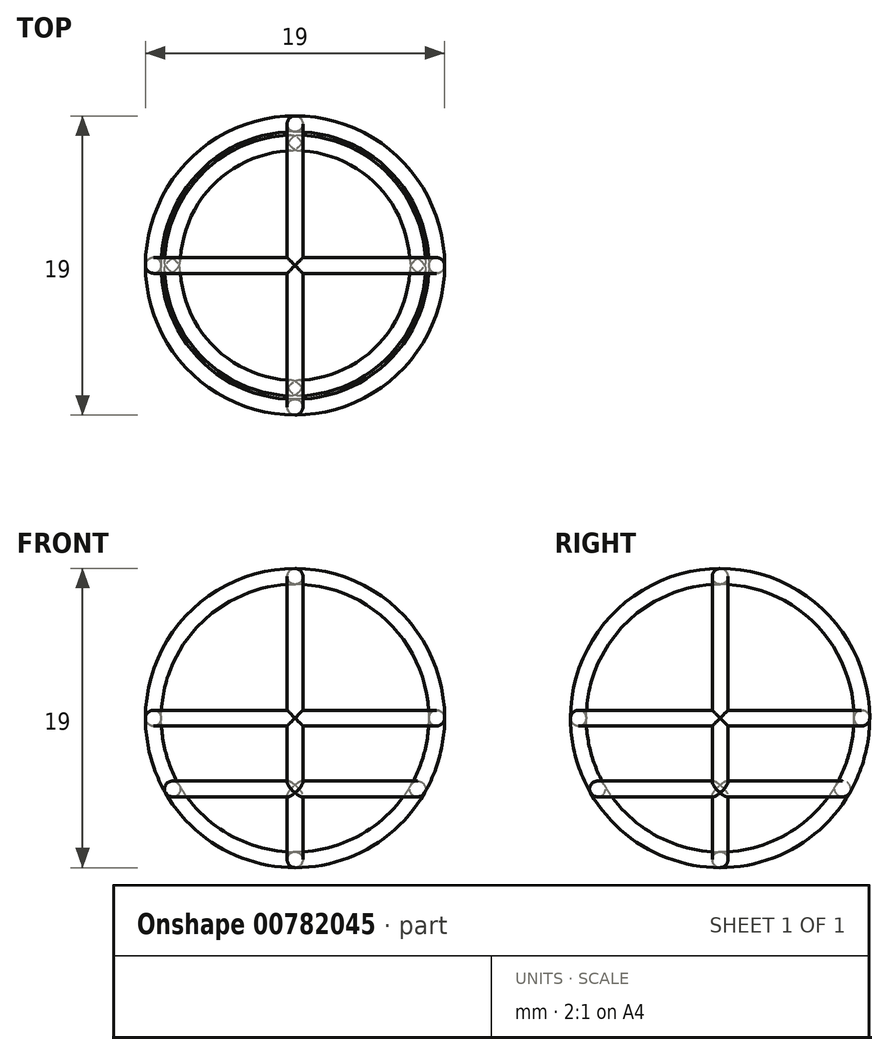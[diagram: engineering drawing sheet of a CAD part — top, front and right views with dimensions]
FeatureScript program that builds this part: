
annotation { "Feature Type Name" : "Feature", "Feature Type Description" : "" }
export const myFeature = defineFeature(function(context is Context, id is Id, definition is map)
    precondition{}
    {
        {
            var Q0;
            Q0=qCreatedBy(makeId("Front.planeOp"),FACE);
            var sketch = newSketch(context, id + "F0", { "sketchPlane" : qUnion([Q0])});
            skCircle(sketch, "E0", {"center": v(0, 0) * mm, "radius": 9 * mm});
            skSolve(sketch);
        }
        {
            var Q0;
            Q0=qCreatedBy(makeId("Right.planeOp"),FACE);
            var sketch = newSketch(context, id + "F1", { "sketchPlane" : qUnion([Q0])});
            skCircle(sketch, "E1", {"center": v(0, 9) * mm, "radius": 0.5 * mm});
            skSolve(sketch);
        }
        {
            var Q0;
            Q0 = qSketchRegion(id + "F1", true);
            var Q1;
            Q1=sQuery(id+"F0.wireOp",EDGE,"E0");
            sweep(context, id + "F2", {"profiles" : qUnion([Q0]), "path" : qUnion([Q1])});
        }
        {
            var Q0;
            Q0=qCreatedBy(makeId("Right.planeOp"),FACE);
            var sketch = newSketch(context, id + "F3", { "sketchPlane" : qUnion([Q0])});
            skCircle(sketch, "E2", {"center": v(0, 0) * mm, "radius": 9 * mm});
            skSolve(sketch);
        }
        {
            var Q0;
            Q0=qCreatedBy(makeId("Front.planeOp"),FACE);
            var sketch = newSketch(context, id + "F4", { "sketchPlane" : qUnion([Q0])});
            skCircle(sketch, "E3", {"center": v(0, 9) * mm, "radius": 0.5 * mm});
            skSolve(sketch);
        }
        {
            var Q0;
            Q0 = qSketchRegion(id + "F4", true);
            var Q1;
            Q1 = qConstructionFilter(qBodyType(qCreatedBy(id + "F3" ,EDGE), BodyType.WIRE), ConstructionObject.NO);
            sweep(context, id + "F5", {"operationType" : NewBodyOperationType.ADD, "profiles" : qUnion([Q0]), "path" : qUnion([Q1])});
        }
        {
            var Q0;
            Q0=qCreatedBy(makeId("Top.planeOp"),FACE);
            var sketch = newSketch(context, id + "F6", { "sketchPlane" : qUnion([Q0])});
            skCircle(sketch, "E4", {"center": v(0, 0) * mm, "radius": 9 * mm});
            skSolve(sketch);
        }
        {
            var Q0;
            Q0=qCreatedBy(makeId("Front.planeOp"),FACE);
            var sketch = newSketch(context, id + "F7", { "sketchPlane" : qUnion([Q0])});
            skCircle(sketch, "E5", {"center": v(9, 0) * mm, "radius": 0.5 * mm});
            skSolve(sketch);
        }
        {
            var Q0;
            Q0 = qSketchRegion(id + "F7", true);
            var Q1;
            Q1 = qConstructionFilter(qBodyType(qCreatedBy(id + "F6" ,EDGE), BodyType.WIRE), ConstructionObject.NO);
            sweep(context, id + "F8", {"operationType" : NewBodyOperationType.ADD, "profiles" : qUnion([Q0]), "path" : qUnion([Q1])});
        }
        {
            var Q0;
            Q0=qCreatedBy(makeId("Top.planeOp"),FACE);
            cPlane(context, id + "F9", {"entities" : qUnion([Q0]), "cplaneType" : CPlaneType.OFFSET, "offset" : 4.5 * mm, "oppositeDirection" : true, "width" : 150 * mm, "height" : 150 * mm});
        }
        {
            var Q0;
            Q0=qCreatedBy(id+"F9.planeOp",FACE);
            var sketch = newSketch(context, id + "F10", { "sketchPlane" : qUnion([Q0])});
            skCircle(sketch, "E6", {"center": v(0, 0) * mm, "radius": 7.8 * mm});
            skSolve(sketch);
        }
        {
            var Q0;
            Q0=qCreatedBy(makeId("Front.planeOp"),FACE);
            var sketch = newSketch(context, id + "F11", { "sketchPlane" : qUnion([Q0])});
            skCircle(sketch, "E7", {"center": v(-7.8, -4.5) * mm, "radius": 0.5 * mm});
            skSolve(sketch);
        }
        {
            var Q0;
            Q0 = qSketchRegion(id + "F11", true);
            var Q1;
            Q1 = qConstructionFilter(qBodyType(qCreatedBy(id + "F10" ,EDGE), BodyType.WIRE), ConstructionObject.NO);
            sweep(context, id + "F12", {"operationType" : NewBodyOperationType.ADD, "profiles" : qUnion([Q0]), "path" : qUnion([Q1])});
        }
    });
